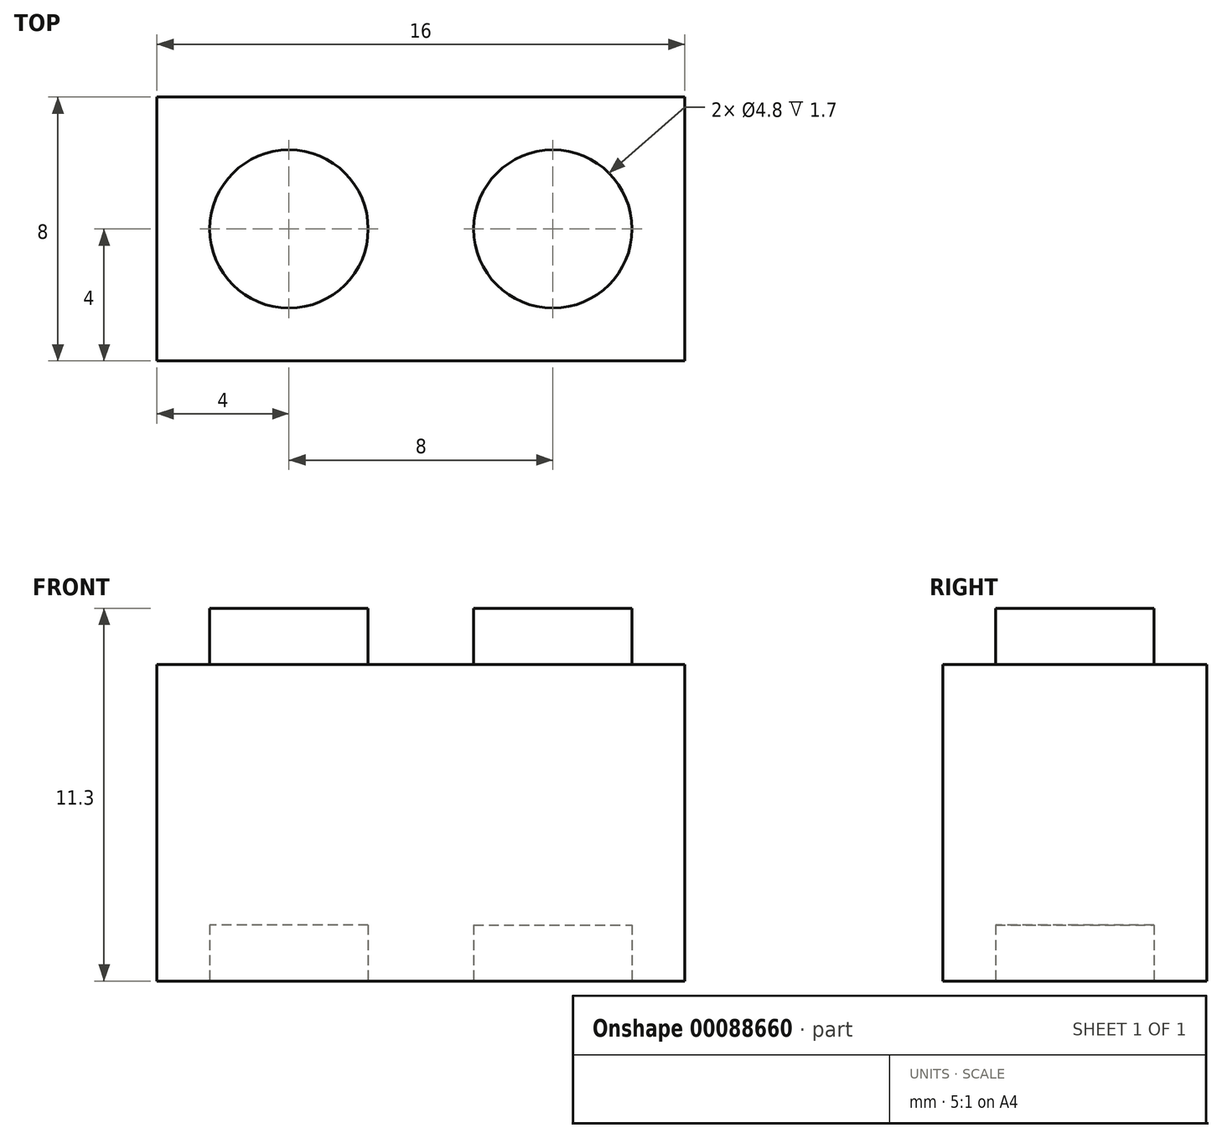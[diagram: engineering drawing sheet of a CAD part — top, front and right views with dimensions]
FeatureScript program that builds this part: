
annotation { "Feature Type Name" : "Feature", "Feature Type Description" : "" }
export const myFeature = defineFeature(function(context is Context, id is Id, definition is map)
    precondition{}
    {
        {
            var Q0;
            Q0=qCreatedBy(makeId("Front.planeOp"),FACE);
            var sketch = newSketch(context, id + "F0", { "sketchPlane" : qUnion([Q0])});
            skLineSegment(sketch, "E0.bottom", {"start": v(-4, 9.6) * mm, "end": v(-2.4, 9.6) * mm});
            skLineSegment(sketch, "E0.top", {"start": v(-4, 0) * mm, "end": v(4, 0) * mm});
            skLineSegment(sketch, "E0.left", {"start": v(-4, 9.6) * mm, "end": v(-4, 0) * mm});
            skLineSegment(sketch, "E0.right", {"start": v(4, 9.6) * mm, "end": v(4, 0) * mm});
            skLineSegment(sketch, "E1.top", {"start": v(-2.4, 11.3) * mm, "end": v(2.4, 11.3) * mm});
            skLineSegment(sketch, "E1.left", {"start": v(-2.4, 9.6) * mm, "end": v(-2.4, 11.3) * mm});
            skLineSegment(sketch, "E1.right", {"start": v(2.4, 9.6) * mm, "end": v(2.4, 11.3) * mm});
            skLineSegment(sketch, "E2", {"start": v(0, 0) * mm, "end": v(0, 24.04) * mm, "construction": true});
            skLineSegment(sketch, "E3.trimOffspring", {"start": v(2.4, 9.6) * mm, "end": v(4, 9.6) * mm});
            skSolve(sketch);
        }
        {
            var Q0;
            Q0=makeQuery(id+"F0.imprint","IMPRINT",FACE,{"disambiguationData":[TD([[makeQuery(id+"F0.imprint","IMPRINT",EDGE,{"derivedFrom":sQuery(id+"F0.wireOp",EDGE,"E0.bottom")}),-1.0]])]});
            extrude(context, id + "F1", {"entities" : qUnion([Q0]), "depth" : 8 * mm});
        }
        {
            var Q0;
            Q0=qCreatedBy(makeId("Top.planeOp"),FACE);
            var Q1;
            Q1=makeQuery(id+"F1.opExtrude","CAP_VERTEX",VERTEX,{"disambiguationData":[OSD([sQuery(id+"F0.wireOp",EDGE,"E1.top"),sQuery(id+"F0.wireOp",EDGE,"E1.right")])],"isStart":true});
            cPlane(context, id + "F2", {"entities" : qUnion([Q0, Q1]), "cplaneType" : CPlaneType.PLANE_POINT, "offset" : 152.4 * mm, "width" : 152.4 * mm, "height" : 152.4 * mm});
        }
        {
            var Q0;
            Q0=qCreatedBy(id+"F2.planeOp",FACE);
            var sketch = newSketch(context, id + "F3", { "sketchPlane" : qUnion([Q0])});
            skLineSegment(sketch, "E4.0", {"start": v(-4, -8) * mm, "end": v(-4, 0) * mm});
            skLineSegment(sketch, "E5.0", {"start": v(4, -8) * mm, "end": v(4, 0) * mm});
            skLineSegment(sketch, "E6", {"start": v(-4, 0) * mm, "end": v(4, 0) * mm});
            skLineSegment(sketch, "E7", {"start": v(-4, -8) * mm, "end": v(4, -8) * mm});
            skLineSegment(sketch, "E8", {"start": v(-4, 0) * mm, "end": v(4, -8) * mm, "construction": true});
            skLineSegment(sketch, "E9", {"start": v(-4, -8) * mm, "end": v(4, 0) * mm, "construction": true});
            skCircle(sketch, "E10", {"center": v(0, -4) * mm, "radius": 2.4 * mm});
            skSolve(sketch);
        }
        {
            var Q0;
            Q0=qSketchRegion(id+"F3",true);
            var Q1;
            Q1=makeQuery(id+"F1.opExtrude","SWEPT_FACE",FACE,{"disambiguationData":[OSD([sQuery(id+"F0.wireOp",EDGE,"E0.bottom")])]});
            extrude(context, id + "F4", {"entities" : qUnion([Q0]), "operationType" : NewBodyOperationType.REMOVE, "endBound" : BoundingType.UP_TO_SURFACE, "oppositeDirection" : true, "endBoundEntityFace" : qUnion([Q1]), "depth" : 25.4 * mm});
        }
        {
            var Q0;
            Q0=qCreatedBy(makeId("Top.planeOp"),FACE);
            var sketch = newSketch(context, id + "F5", { "sketchPlane" : qUnion([Q0])});
            skCircle(sketch, "E11.0", {"center": v(0, -4) * mm, "radius": 2.4 * mm});
            skSolve(sketch);
        }
        {
            var Q0;
            Q0=makeQuery(id+"F5.imprint","IMPRINT",FACE,{"disambiguationData":[TD([[makeQuery(id+"F5.imprint","IMPRINT",EDGE,{"derivedFrom":sQuery(id+"F5.wireOp",EDGE,"E11.0")}),1.0]])]});
            extrude(context, id + "F6", {"entities" : qUnion([Q0]), "operationType" : NewBodyOperationType.REMOVE, "depth" : 1.7 * mm});
        }
        {
            var Q0;
            Q0=qCreatedBy(makeId("Right.planeOp"),FACE);
            var Q1;
            Q1=makeQuery(id+"F1.opExtrude","CAP_VERTEX",VERTEX,{"disambiguationData":[OSD([sQuery(id+"F0.wireOp",EDGE,"E0.right"),sQuery(id+"F0.wireOp",EDGE,"E3.trimOffspring")])],"isStart":false});
            cPlane(context, id + "F7", {"entities" : qUnion([Q0, Q1]), "cplaneType" : CPlaneType.PLANE_POINT, "offset" : 152.4 * mm, "width" : 152.4 * mm, "height" : 152.4 * mm});
        }
        {
            var Q0;
            Q0=makeQuery(id+"F1.opExtrude","SWEPT_BODY",BODY,{"disambiguationData":[OSD([sQuery(id+"F0.wireOp",EDGE,"E0.bottom"),sQuery(id+"F0.wireOp",EDGE,"E0.top"),sQuery(id+"F0.wireOp",EDGE,"E0.left"),sQuery(id+"F0.wireOp",EDGE,"E0.right"),sQuery(id+"F0.wireOp",EDGE,"E1.top"),sQuery(id+"F0.wireOp",EDGE,"E1.left"),sQuery(id+"F0.wireOp",EDGE,"E1.right"),sQuery(id+"F0.wireOp",EDGE,"E3.trimOffspring")])]});
            var Q1;
            Q1=qCreatedBy(id+"F7.planeOp",FACE);
            mirror(context, id + "F8", {"operationType" : NewBodyOperationType.ADD, "entities" : qUnion([Q0]), "mirrorPlane" : qUnion([Q1])});
        }
    });
